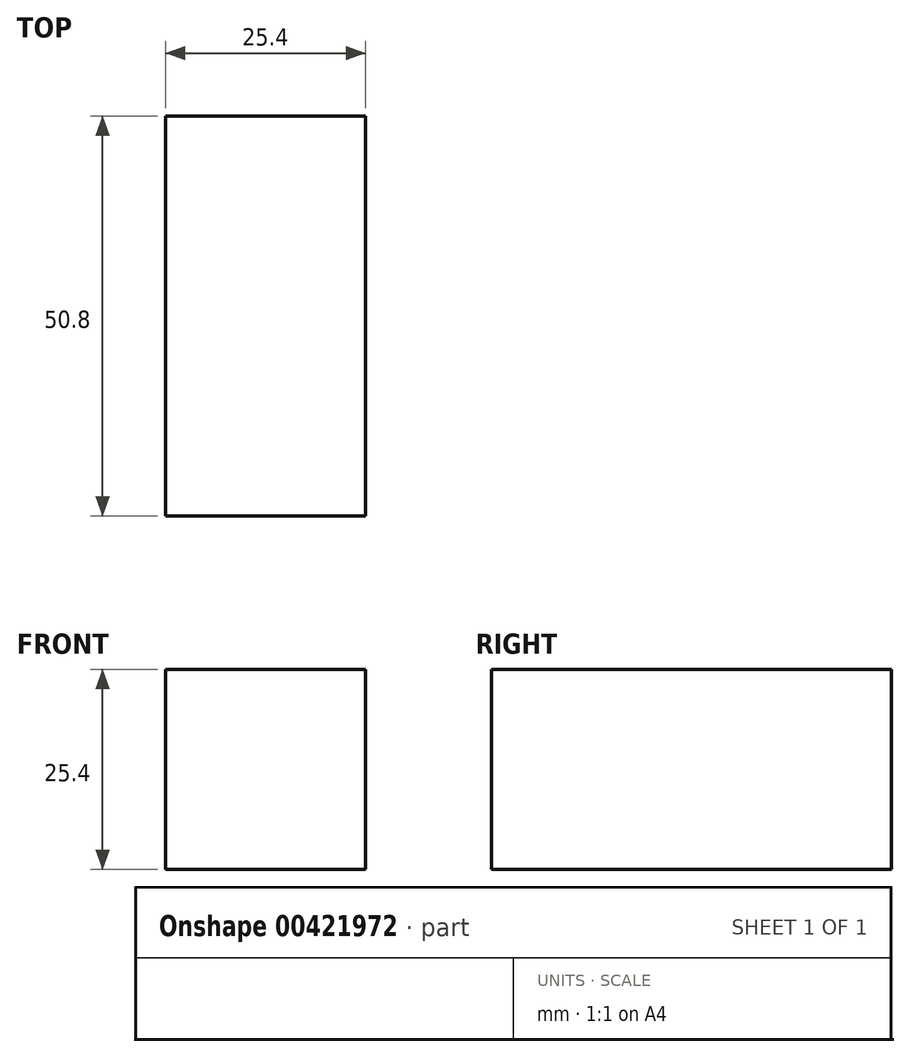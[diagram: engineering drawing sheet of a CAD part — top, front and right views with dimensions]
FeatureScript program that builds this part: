
annotation { "Feature Type Name" : "Feature", "Feature Type Description" : "" }
export const myFeature = defineFeature(function(context is Context, id is Id, definition is map)
    precondition{}
    {
        {
            var Q0;
            Q0=qCreatedBy(makeId("Front.planeOp"),FACE);
            var sketch = newSketch(context, id + "F0", { "sketchPlane" : qUnion([Q0])});
            skLineSegment(sketch, "E0.bottom", {"start": v(-8.79, 20.63) * mm, "end": v(16.61, 20.63) * mm});
            skLineSegment(sketch, "E0.top", {"start": v(-8.79, -4.77) * mm, "end": v(16.61, -4.77) * mm});
            skLineSegment(sketch, "E0.left", {"start": v(-8.79, 20.63) * mm, "end": v(-8.79, -4.77) * mm});
            skLineSegment(sketch, "E0.right", {"start": v(16.61, 20.63) * mm, "end": v(16.61, -4.77) * mm});
            skSolve(sketch);
        }
        {
            var Q0;
            Q0=makeQuery(id+"F0.imprint","IMPRINT",FACE,{"disambiguationData":[TD([[makeQuery(id+"F0.imprint","IMPRINT",EDGE,{"derivedFrom":sQuery(id+"F0.wireOp",EDGE,"E0.bottom")}),-1.0]])]});
            extrude(context, id + "F1", {"entities" : qUnion([Q0]), "depth" : 50.8 * mm});
        }
    });
